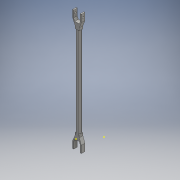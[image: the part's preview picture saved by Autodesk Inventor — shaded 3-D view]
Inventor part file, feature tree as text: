
AUTODESK INVENTOR PART (.ipt)
format: ipt  version: 2016 (Build 200138000, 138)  size: 188,416 bytes
history: native  units: mm
features: sketch x8, extrude x6
ambient origin geometry x8: Origin, YZ Plane, XZ Plane, XY Plane, X Axis, Y Axis, Z Axis, Center Point
bodies: Solid1 (feature_tree)
feature tree (14):
  extrude  "Extrusion1"  Depth=164.0mm TaperAngle=0.0deg
  extrude  "Extrusion2"  Depth=2.0mm
  sketch  "Sketch3"  dims[d16=27.824719mm d17=11.0mm]
  extrude  "Extrusion3"  Depth=11.0mm
  extrude  "Extrusion4"  Depth=6.5mm TaperAngle=0.0deg
  extrude  "Extrusion5"  Depth=6.5mm
  extrude  "Extrusion6"  Depth=6.5mm TaperAngle=0.0deg
  sketch  "Sketch9"  dims[d32=2.0mm d34=2.0mm d35=2.0mm d36=11.0mm d37=12.0mm d38=2.0mm d39=2.0mm d40=6.5mm d41=0.0mm d42=6.5mm d43=0.0mm]
  sketch  "Sketch1"  dims[d0=7.5mm d1=164.0mm d2=0.0mm]
  sketch  "Sketch2"  dims[d12=2.0mm d13=2.0mm]
  sketch  "Sketch5"  dims[d21=12.0mm d22=6.5mm d23=0.0mm]
  sketch  "Sketch6"  dims[d25=6.5mm d26=0.0mm d27=6.0mm]
  sketch  "Sketch7"  dims[d28=3.0mm d29=6.5mm d30=0.0mm]
  sketch  "Sketch8"  dims[d31=2.0mm]
